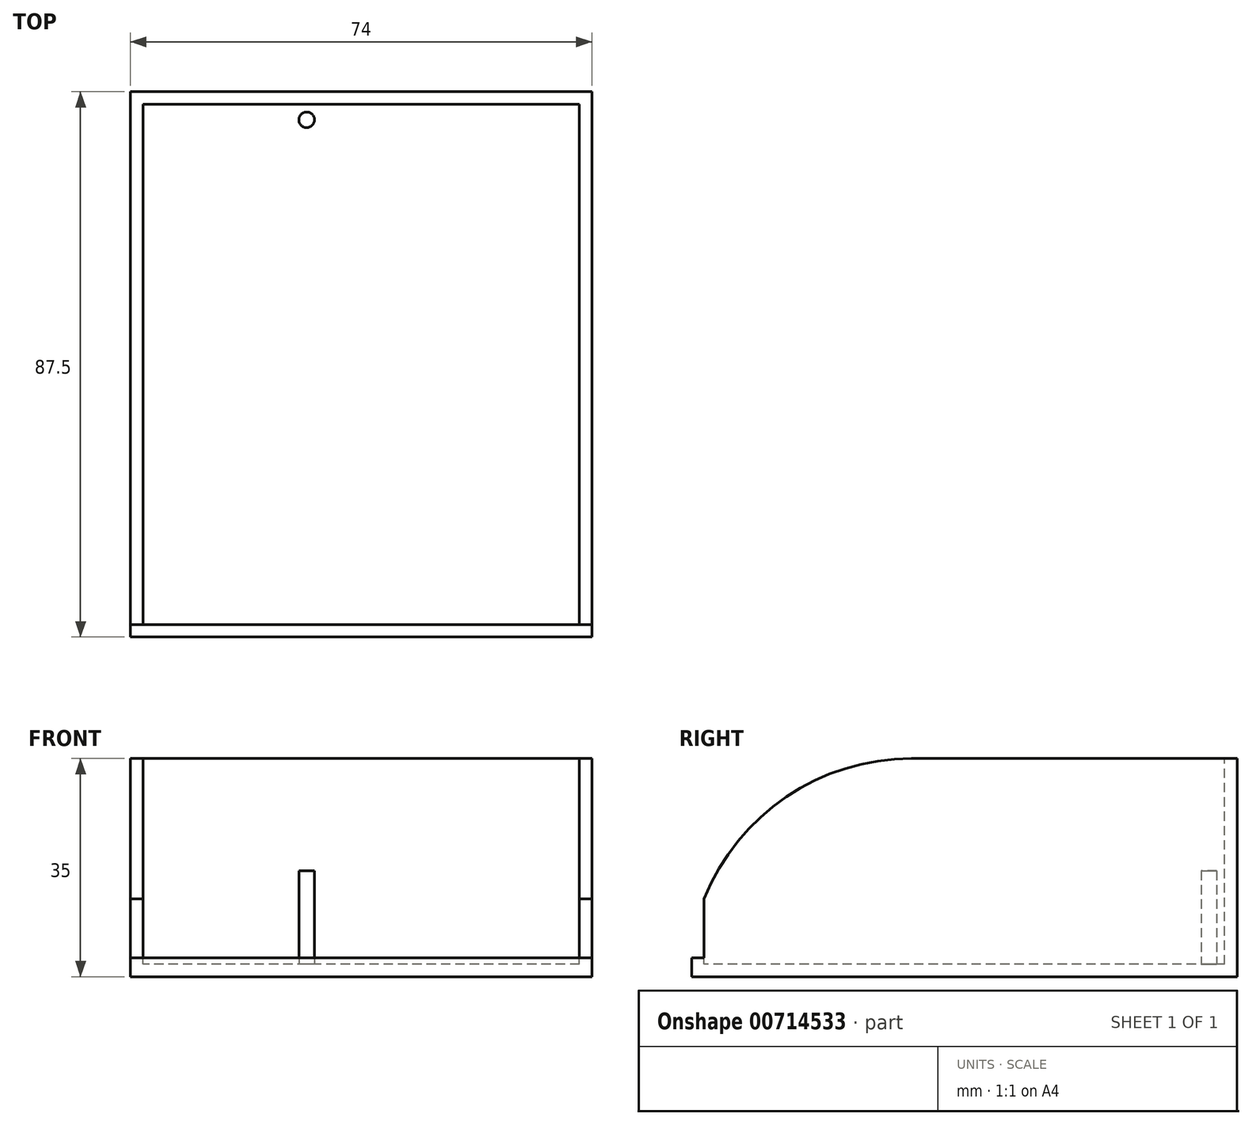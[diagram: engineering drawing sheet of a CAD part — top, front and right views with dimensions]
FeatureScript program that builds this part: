
annotation { "Feature Type Name" : "Feature", "Feature Type Description" : "" }
export const myFeature = defineFeature(function(context is Context, id is Id, definition is map)
    precondition{}
    {
        {
            var Q0;
            Q0=qCreatedBy(makeId("Top.planeOp"),FACE);
            var sketch = newSketch(context, id + "F0", { "sketchPlane" : qUnion([Q0])});
            skLineSegment(sketch, "E0.bottom", {"start": v(37, 43.75) * mm, "end": v(-37, 43.75) * mm});
            skLineSegment(sketch, "E0.top", {"start": v(37, -43.75) * mm, "end": v(-37, -43.75) * mm});
            skLineSegment(sketch, "E0.left", {"start": v(37, 43.75) * mm, "end": v(37, -43.75) * mm});
            skLineSegment(sketch, "E0.right", {"start": v(-37, 43.75) * mm, "end": v(-37, -43.75) * mm});
            skPoint(sketch, "E0.middle", {"position": v(0, 0) * mm});
            skSolve(sketch);
        }
        {
            var Q0;
            Q0=qSketchRegion(id+"F0",true);
            extrude(context, id + "F1", {"entities" : qUnion([Q0]), "depth" : 34 * mm, "offsetDistance" : 25 * mm});
        }
        {
            var Q0;
            Q0=makeQuery(id+"F1.opExtrude","CAP_FACE",FACE,{"disambiguationData":[OSD([sQuery(id+"F0.wireOp",EDGE,"E0.bottom"),sQuery(id+"F0.wireOp",EDGE,"E0.top"),sQuery(id+"F0.wireOp",EDGE,"E0.left"),sQuery(id+"F0.wireOp",EDGE,"E0.right")])],"isStart":false});
            var sketch = newSketch(context, id + "F2", { "sketchPlane" : qUnion([Q0])});
            skLineSegment(sketch, "E1.bottom", {"start": v(35, 41.75) * mm, "end": v(-35, 41.75) * mm});
            skLineSegment(sketch, "E1.top", {"start": v(35, -41.75) * mm, "end": v(-35, -41.75) * mm});
            skLineSegment(sketch, "E1.left", {"start": v(35, 41.75) * mm, "end": v(35, -41.75) * mm});
            skLineSegment(sketch, "E1.right", {"start": v(-35, 41.75) * mm, "end": v(-35, -41.75) * mm});
            skPoint(sketch, "E1.middle", {"position": v(0, 0) * mm});
            skSolve(sketch);
        }
        {
            var Q0;
            Q0=makeQuery(id+"F1.opExtrude","SWEPT_FACE",FACE,{"disambiguationData":[OSD([sQuery(id+"F0.wireOp",EDGE,"E0.right")])]});
            var sketch = newSketch(context, id + "F3", { "sketchPlane" : qUnion([Q0])});
            skLineSegment(sketch, "E2", {"start": v(-43.75, 0) * mm, "end": v(-41.75, 0) * mm});
            skLineSegment(sketch, "E3", {"start": v(-41.75, 0) * mm, "end": v(8.5, 0) * mm});
            skLineSegment(sketch, "E4", {"start": v(8.5, 0) * mm, "end": v(39.75, 0) * mm});
            skLineSegment(sketch, "E5", {"start": v(39.75, 0) * mm, "end": v(43.75, 0) * mm});
            skLineSegment(sketch, "E6", {"start": v(-43.75, 0) * mm, "end": v(-43.75, 2) * mm});
            skLineSegment(sketch, "E7", {"start": v(-43.75, 2) * mm, "end": v(-41.75, 2) * mm});
            skLineSegment(sketch, "E8", {"start": v(-41.75, 2) * mm, "end": v(8.5, 2) * mm});
            skLineSegment(sketch, "E9.top", {"start": v(-41.75, 34) * mm, "end": v(8.5, 34) * mm});
            skLineSegment(sketch, "E9.left", {"start": v(-41.75, 2) * mm, "end": v(-41.75, 34) * mm});
            skLineSegment(sketch, "E9.right", {"start": v(8.5, 2) * mm, "end": v(8.5, 34) * mm});
            skLineSegment(sketch, "E10", {"start": v(8.5, 2) * mm, "end": v(41.75, 2) * mm});
            skLineSegment(sketch, "E11", {"start": v(41.75, 2) * mm, "end": v(43.75, 2) * mm});
            skLineSegment(sketch, "E12", {"start": v(41.75, 2) * mm, "end": v(41.75, 34) * mm});
            skLineSegment(sketch, "E13", {"start": v(41.75, 34) * mm, "end": v(8.5, 34) * mm});
            skLineSegment(sketch, "E14", {"start": v(43.75, 2) * mm, "end": v(43.75, 11.5) * mm});
            skLineSegment(sketch, "E15.bottom", {"start": v(43.75, 11.5) * mm, "end": v(41.75, 11.5) * mm});
            skLineSegment(sketch, "E15.top", {"start": v(43.75, 2) * mm, "end": v(41.75, 2) * mm});
            skLineSegment(sketch, "E15.left", {"start": v(43.75, 11.5) * mm, "end": v(43.75, 2) * mm});
            skLineSegment(sketch, "E15.right", {"start": v(41.75, 11.5) * mm, "end": v(41.75, 2) * mm});
            skLineSegment(sketch, "E16", {"start": v(41.75, 11.5) * mm, "end": v(8.5, 11.5) * mm});
            skArc(sketch, "E17", {"start": v(41.75, 11.5) * mm, "mid": v(28.57, 27.85) * mm, "end": v(8.5, 34) * mm});
            skSolve(sketch);
        }
        {
            var Q0;
            Q0=qSketchRegion(id+"F2",true);
            extrude(context, id + "F4", {"entities" : qUnion([Q0]), "operationType" : NewBodyOperationType.REMOVE, "oppositeDirection" : true, "depth" : 33 * mm, "offsetDistance" : 25 * mm});
        }
        {
            var Q0;
            Q0=makeQuery(id+"F3.imprint","IMPRINT",FACE,{"disambiguationData":[TD([[makeQuery(id+"F3.imprint","IMPRINT",EDGE,{"derivedFrom":sQuery(id+"F3.wireOp",EDGE,"E12")}),1.0]])]});
            var Q1;
            {var subQ0=sQuery(id+"F3.wireOp",EDGE,"E12");Q1=makeQuery(id+"F3.imprint","IMPRINT",FACE,{"disambiguationData":[TD([[makeQuery(id+"F3.imprint","IMPRINT",EDGE,{"derivedFrom":subQ0}),-1.0]])]});}
            extrude(context, id + "F5", {"entities" : qUnion([Q0, Q1]), "operationType" : NewBodyOperationType.REMOVE, "oppositeDirection" : true, "depth" : 74 * mm, "offsetDistance" : 25 * mm});
        }
        {
            var Q0;
            Q0=makeQuery(id+"F1.opExtrude","SWEPT_FACE",FACE,{"disambiguationData":[OSD([sQuery(id+"F0.wireOp",EDGE,"E0.top")])]});
            var sketch = newSketch(context, id + "F6", { "sketchPlane" : qUnion([Q0])});
            skLineSegment(sketch, "E18.bottom", {"start": v(-37, 0) * mm, "end": v(-35, 0) * mm});
            skLineSegment(sketch, "E18.top", {"start": v(-37, 2) * mm, "end": v(-35, 2) * mm});
            skLineSegment(sketch, "E18.left", {"start": v(-37, 0) * mm, "end": v(-37, 2) * mm});
            skLineSegment(sketch, "E18.right", {"start": v(-35, 0) * mm, "end": v(-35, 2) * mm});
            skLineSegment(sketch, "E19", {"start": v(-35, 2) * mm, "end": v(-15, 2) * mm});
            skLineSegment(sketch, "E20", {"start": v(-15, 2) * mm, "end": v(-7, 2) * mm});
            skLineSegment(sketch, "E21", {"start": v(-7, 2) * mm, "end": v(37, 2) * mm});
            skLineSegment(sketch, "E22.bottom", {"start": v(-37, 2) * mm, "end": v(0, 2) * mm});
            skLineSegment(sketch, "E22.top", {"start": v(-37, 0) * mm, "end": v(0, 0) * mm});
            skLineSegment(sketch, "E22.left", {"start": v(-37, 2) * mm, "end": v(-37, 0) * mm});
            skLineSegment(sketch, "E22.right", {"start": v(0, 2) * mm, "end": v(0, 0) * mm});
            skLineSegment(sketch, "E23", {"start": v(-7, 2) * mm, "end": v(-7, 11.5) * mm});
            skLineSegment(sketch, "E24.bottom", {"start": v(-7, 11.5) * mm, "end": v(-17, 11.5) * mm});
            skLineSegment(sketch, "E24.top", {"start": v(-7, 8.5) * mm, "end": v(-17, 8.5) * mm});
            skLineSegment(sketch, "E24.left", {"start": v(-7, 11.5) * mm, "end": v(-7, 8.5) * mm});
            skLineSegment(sketch, "E24.right", {"start": v(-17, 11.5) * mm, "end": v(-17, 8.5) * mm});
            skSolve(sketch);
        }
        {
            var Q0;
            Q0=makeQuery(id+"F4.boolean.opBoolean","COPY",FACE,{"derivedFrom":makeQuery(id+"F4.opExtrude","CAP_FACE",FACE,{"disambiguationData":[OSD([sQuery(id+"F2.wireOp",EDGE,"E1.bottom"),sQuery(id+"F2.wireOp",EDGE,"E1.top"),sQuery(id+"F2.wireOp",EDGE,"E1.left"),sQuery(id+"F2.wireOp",EDGE,"E1.right")])],"isStart":false})});
            var sketch = newSketch(context, id + "F7", { "sketchPlane" : qUnion([Q0])});
            skLineSegment(sketch, "E25.bottom", {"start": v(-35, 41.75) * mm, "end": v(-8.75, 41.75) * mm});
            skLineSegment(sketch, "E25.top", {"start": v(-35, 39.25) * mm, "end": v(-8.75, 39.25) * mm});
            skLineSegment(sketch, "E25.left", {"start": v(-35, 41.75) * mm, "end": v(-35, 39.25) * mm});
            skLineSegment(sketch, "E25.right", {"start": v(-8.75, 41.75) * mm, "end": v(-8.75, 39.25) * mm});
            skCircle(sketch, "E26", {"center": v(-8.75, 39.25) * mm, "radius": 1.25 * mm});
            skSolve(sketch);
        }
        {
            var Q0;
            {var subQ0=sQuery(id+"F7.wireOp",EDGE,"E25.right");var subQ1=sQuery(id+"F7.wireOp",EDGE,"E25.top");var subQ2=makeQuery(id+"F7.imprint","INTERSECT",VERTEX,{"derivedFrom":[subQ1,subQ0]});Q0=makeQuery(id+"F7.imprint","IMPRINT",FACE,{"disambiguationData":[TD([[makeQuery(id+"F7.imprint","IMPRINT",EDGE,{"disambiguationData":[TD([[subQ2,1.0]])],"derivedFrom":subQ1}),-1.0]])]});}
            var Q1;
            {var subQ0=sQuery(id+"F7.wireOp",EDGE,"E25.right");var subQ1=sQuery(id+"F7.wireOp",EDGE,"E25.top");var subQ2=makeQuery(id+"F7.imprint","INTERSECT",VERTEX,{"derivedFrom":[subQ1,subQ0]});Q1=makeQuery(id+"F7.imprint","IMPRINT",FACE,{"disambiguationData":[TD([[makeQuery(id+"F7.imprint","IMPRINT",EDGE,{"disambiguationData":[TD([[subQ2,1.0]])],"derivedFrom":subQ1}),1.0]])]});}
            extrude(context, id + "F8", {"entities" : qUnion([Q0, Q1]), "operationType" : NewBodyOperationType.ADD, "depth" : 15 * mm, "offsetDistance" : 25 * mm});
        }
        {
            var Q0;
            Q0 = qSketchRegion(id + "F0", true);
            var Q1;
            Q1=makeQuery(id+"F0.imprint","IMPRINT",FACE,{"disambiguationData":[TD([[makeQuery(id+"F0.imprint","IMPRINT",EDGE,{"derivedFrom":sQuery(id+"F0.wireOp",EDGE,"E0.bottom")}),1.0]])]});
            extrude(context, id + "F9", {"entities" : qUnion([Q0, Q1]), "operationType" : NewBodyOperationType.ADD, "oppositeDirection" : true, "depth" : 1 * mm, "offsetDistance" : 25 * mm});
        }
        {
            var Q0;
            Q0=makeQuery(id+"F6.imprint","IMPRINT",FACE,{"disambiguationData":[TD([[makeQuery(id+"F6.imprint","IMPRINT",EDGE,{"derivedFrom":sQuery(id+"F6.wireOp",EDGE,"E24.bottom")}),1.0]])]});
            extrude(context, id + "F10", {"entities" : qUnion([Q0]), "operationType" : NewBodyOperationType.REMOVE, "oppositeDirection" : true, "depth" : 4 * mm, "offsetDistance" : 25 * mm});
        }
    });
